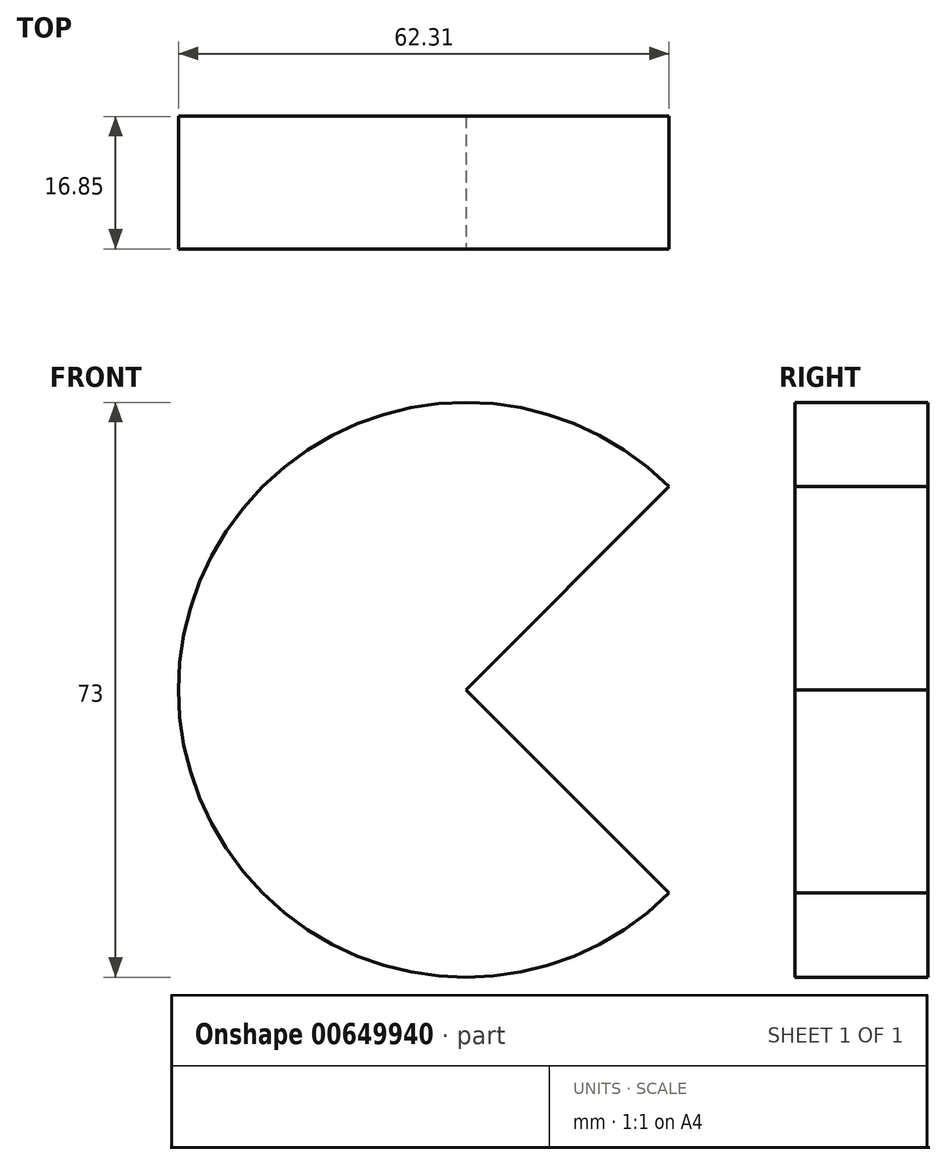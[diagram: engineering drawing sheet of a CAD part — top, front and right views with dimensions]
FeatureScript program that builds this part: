
annotation { "Feature Type Name" : "Feature", "Feature Type Description" : "" }
export const myFeature = defineFeature(function(context is Context, id is Id, definition is map)
    precondition{}
    {
        {
            var Q0;
            Q0=qCreatedBy(makeId("Top.planeOp"),FACE);
            var sketch = newSketch(context, id + "F0", { "sketchPlane" : qUnion([Q0])});
            skLineSegment(sketch, "E0.bottom", {"start": v(-36.5, 16.85) * mm, "end": v(0, 16.85) * mm});
            skLineSegment(sketch, "E0.top", {"start": v(-36.5, 0) * mm, "end": v(0, 0) * mm});
            skLineSegment(sketch, "E0.left", {"start": v(-36.5, 16.85) * mm, "end": v(-36.5, 0) * mm});
            skLineSegment(sketch, "E0.right", {"start": v(0, 16.85) * mm, "end": v(0, 0) * mm});
            skSolve(sketch);
        }
        {
            var Q0;
            Q0=makeQuery(id+"F0.imprint","IMPRINT",FACE,{"disambiguationData":[TD([[makeQuery(id+"F0.imprint","IMPRINT",EDGE,{"derivedFrom":sQuery(id+"F0.wireOp",EDGE,"E0.bottom")}),-1.0]])]});
            var Q1;
            Q1=sQuery(id+"F0.wireOp",EDGE,"E0.right");
            revolve(context, id + "F1", {"entities" : qUnion([Q0]), "axis" : qUnion([Q1]), "revolveType" : RevolveType.TWO_DIRECTIONS, "angle" : 135 * degree, "angleBack" : 225 * degree});
        }
    });
